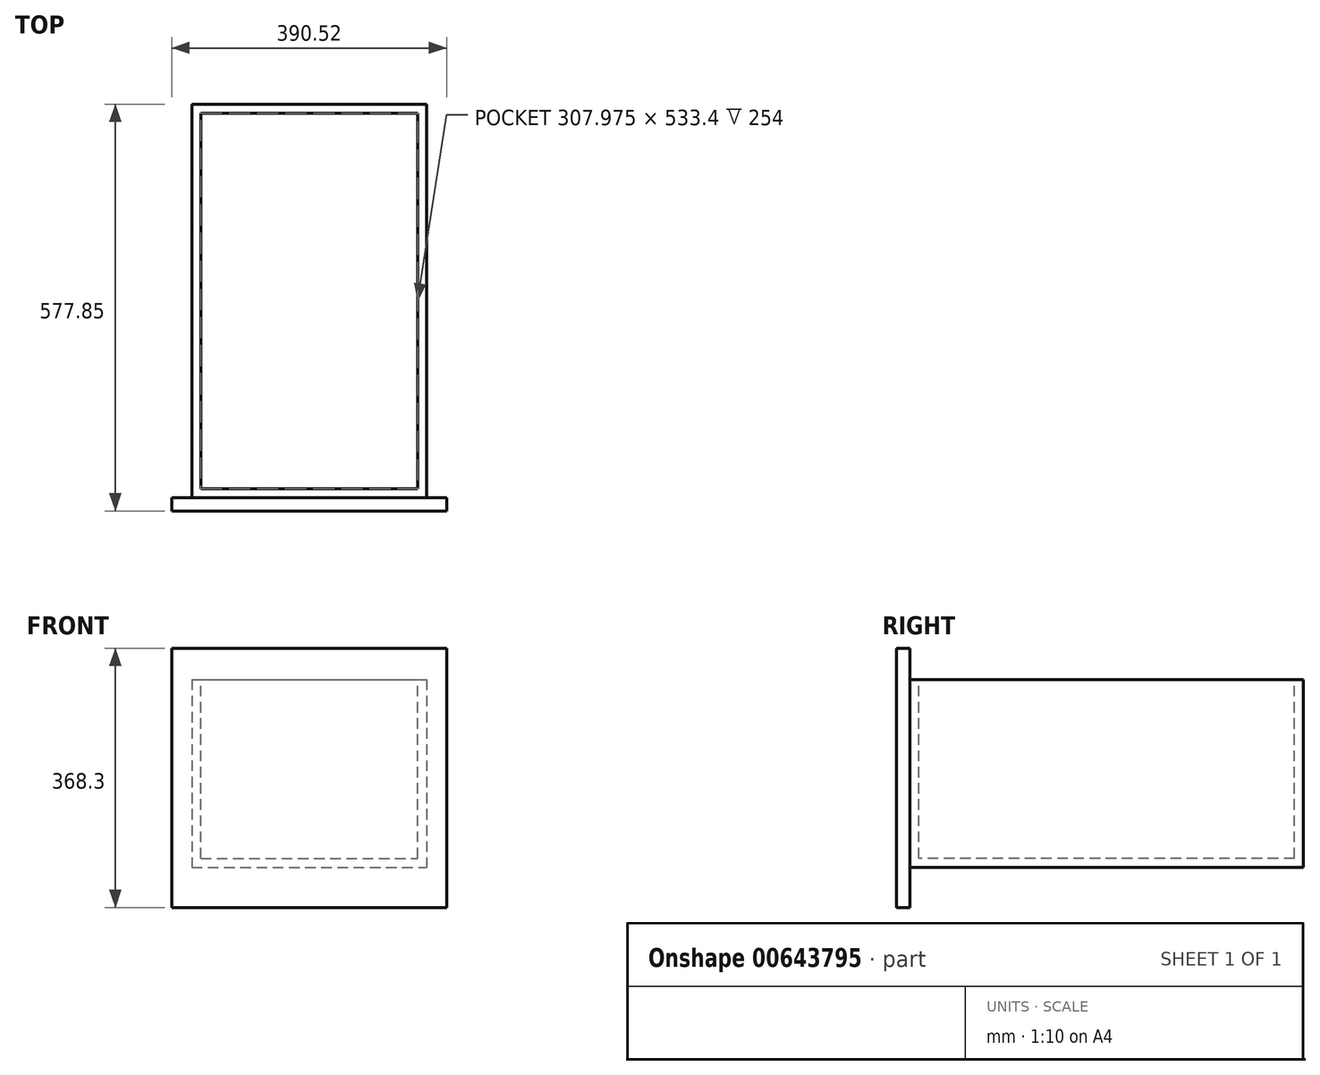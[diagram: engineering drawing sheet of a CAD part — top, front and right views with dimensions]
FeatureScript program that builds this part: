
annotation { "Feature Type Name" : "Feature", "Feature Type Description" : "" }
export const myFeature = defineFeature(function(context is Context, id is Id, definition is map)
    precondition{}
    {
        {
            var Q0;
            Q0=qCreatedBy(makeId("Front.planeOp"),FACE);
            var sketch = newSketch(context, id + "F0", { "sketchPlane" : qUnion([Q0])});
            skLineSegment(sketch, "E0.bottom", {"start": v(-195.26, 184.15) * mm, "end": v(195.26, 184.15) * mm});
            skLineSegment(sketch, "E0.top", {"start": v(-195.26, -184.15) * mm, "end": v(195.26, -184.15) * mm});
            skLineSegment(sketch, "E0.left", {"start": v(-195.26, 184.15) * mm, "end": v(-195.26, -184.15) * mm});
            skLineSegment(sketch, "E0.right", {"start": v(195.26, 184.15) * mm, "end": v(195.26, -184.15) * mm});
            skPoint(sketch, "E0.middle", {"position": v(0, 0) * mm});
            skSolve(sketch);
        }
        {
            var Q0;
            Q0=makeQuery(id+"F0.imprint","IMPRINT",FACE,{"disambiguationData":[TD([[makeQuery(id+"F0.imprint","IMPRINT",EDGE,{"derivedFrom":sQuery(id+"F0.wireOp",EDGE,"E0.bottom")}),-1.0]])]});
            extrude(context, id + "F1", {"entities" : qUnion([Q0]), "depth" : 19.05 * mm, "offsetDistance" : 25.4 * mm});
        }
        {
            var Q0;
            Q0=makeQuery(id+"F1.opExtrude","CAP_FACE",FACE,{"disambiguationData":[OSD([sQuery(id+"F0.wireOp",EDGE,"E0.bottom"),sQuery(id+"F0.wireOp",EDGE,"E0.top"),sQuery(id+"F0.wireOp",EDGE,"E0.left"),sQuery(id+"F0.wireOp",EDGE,"E0.right")])],"isStart":true});
            var sketch = newSketch(context, id + "F2", { "sketchPlane" : qUnion([Q0])});
            skLineSegment(sketch, "E1", {"start": v(0, -184.15) * mm, "end": v(0, -139.7) * mm});
            skPoint(sketch, "E1.endSnap0", {"position": v(0, -184.15) * mm});
            skLineSegment(sketch, "E2", {"start": v(0, -139.7) * mm, "end": v(0, -127) * mm});
            skLineSegment(sketch, "E3", {"start": v(0, -127) * mm, "end": v(0, 6.35) * mm});
            skLineSegment(sketch, "E4.bottom", {"start": v(166.69, 139.7) * mm, "end": v(-166.69, 139.7) * mm});
            skLineSegment(sketch, "E4.top", {"start": v(166.69, -127) * mm, "end": v(-166.69, -127) * mm});
            skLineSegment(sketch, "E4.left", {"start": v(166.69, 139.7) * mm, "end": v(166.69, -127) * mm});
            skLineSegment(sketch, "E4.right", {"start": v(-166.69, 139.7) * mm, "end": v(-166.69, -127) * mm});
            skPoint(sketch, "E4.middle", {"position": v(0, 6.35) * mm});
            skSolve(sketch);
        }
        {
            var Q0;
            Q0=makeQuery(id+"F2.imprint","IMPRINT",FACE,{"disambiguationData":[TD([[makeQuery(id+"F2.imprint","IMPRINT",EDGE,{"derivedFrom":sQuery(id+"F2.wireOp",EDGE,"E4.bottom")}),1.0]])]});
            extrude(context, id + "F3", {"entities" : qUnion([Q0]), "operationType" : NewBodyOperationType.ADD, "depth" : 558.8 * mm, "offsetDistance" : 25.4 * mm});
        }
        {
            var Q0;
            Q0=makeQuery(id+"F3.opExtrude","SWEPT_FACE",FACE,{"disambiguationData":[OSD([sQuery(id+"F2.wireOp",EDGE,"E4.bottom")])]});
            var sketch = newSketch(context, id + "F4", { "sketchPlane" : qUnion([Q0])});
            skLineSegment(sketch, "E5.bottom", {"start": v(-153.99, 546.1) * mm, "end": v(153.99, 546.1) * mm});
            skLineSegment(sketch, "E5.top", {"start": v(-153.99, 12.7) * mm, "end": v(153.99, 12.7) * mm});
            skLineSegment(sketch, "E5.left", {"start": v(-153.99, 546.1) * mm, "end": v(-153.99, 12.7) * mm});
            skLineSegment(sketch, "E5.right", {"start": v(153.99, 546.1) * mm, "end": v(153.99, 12.7) * mm});
            skPoint(sketch, "E5.middle", {"position": v(0, 279.4) * mm});
            skPoint(sketch, "E5.middle.positionSnap0", {"position": v(-166.69, 279.4) * mm});
            skPoint(sketch, "E5.centerSnap0", {"position": v(-166.69, 279.4) * mm});
            skSolve(sketch);
        }
        {
            var Q0;
            Q0=makeQuery(id+"F4.imprint","IMPRINT",FACE,{"disambiguationData":[TD([[makeQuery(id+"F4.imprint","IMPRINT",EDGE,{"derivedFrom":sQuery(id+"F4.wireOp",EDGE,"E5.bottom")}),-1.0]])]});
            extrude(context, id + "F5", {"entities" : qUnion([Q0]), "operationType" : NewBodyOperationType.REMOVE, "oppositeDirection" : true, "depth" : 254 * mm, "offsetDistance" : 25.4 * mm});
        }
    });
